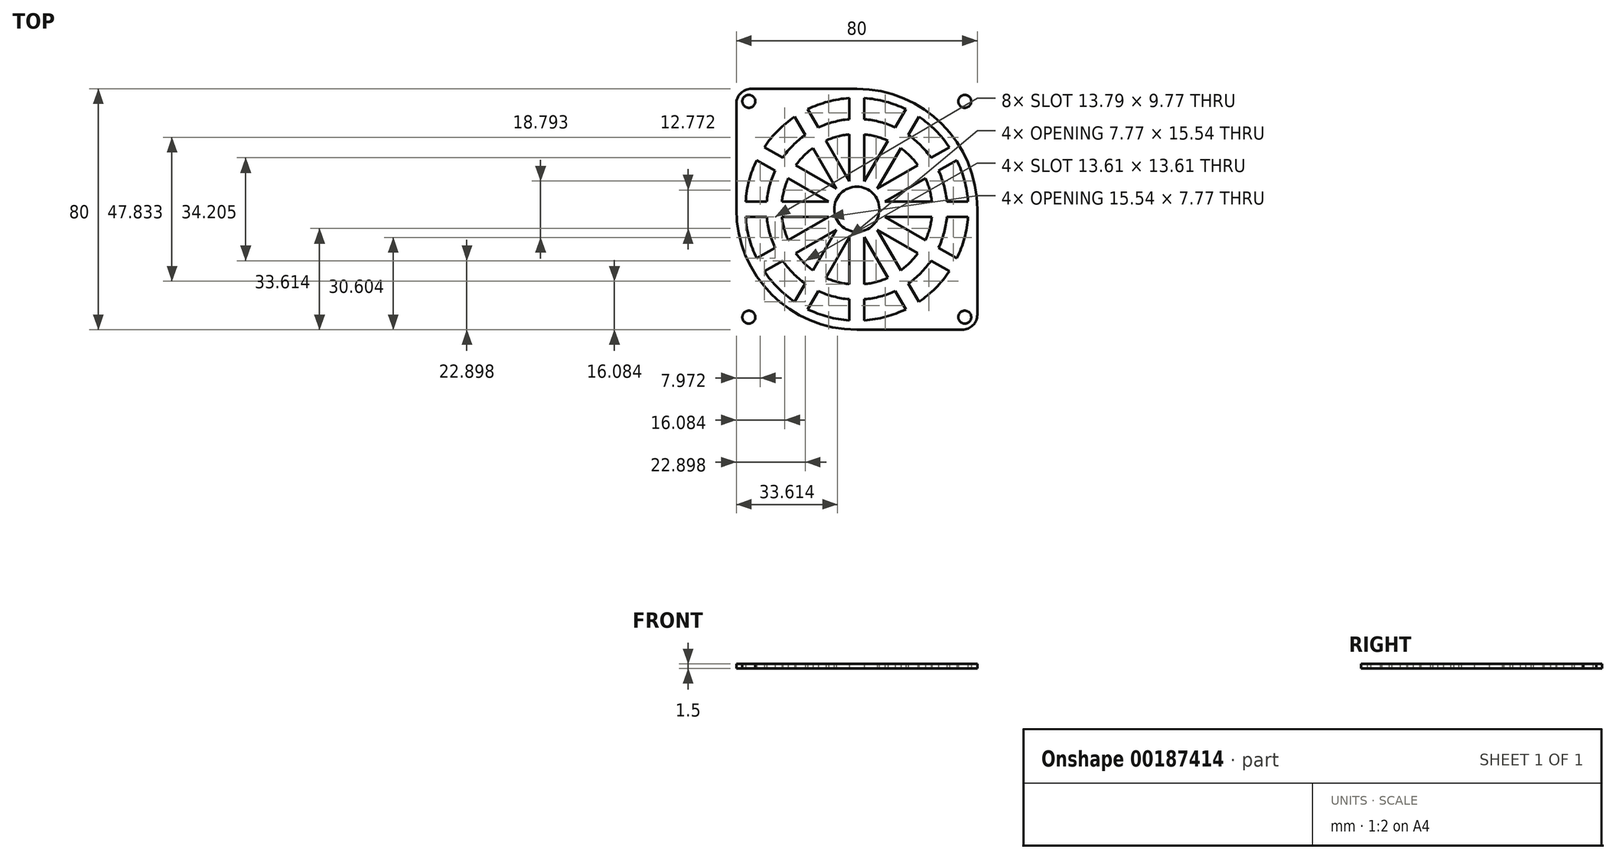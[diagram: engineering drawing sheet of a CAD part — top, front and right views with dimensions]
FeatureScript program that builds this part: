
annotation { "Feature Type Name" : "Feature", "Feature Type Description" : "" }
export const myFeature = defineFeature(function(context is Context, id is Id, definition is map)
    precondition{}
    {
        {
            var Q0;
            Q0=qCreatedBy(makeId("Top.planeOp"),FACE);
            var sketch = newSketch(context, id + "F0", { "sketchPlane" : qUnion([Q0])});
            skLineSegment(sketch, "E0.bottom", {"start": v(-35, 40) * mm, "end": v(35, 40) * mm});
            skLineSegment(sketch, "E0.top", {"start": v(-35, -40) * mm, "end": v(35, -40) * mm});
            skLineSegment(sketch, "E0.left", {"start": v(-40, 35) * mm, "end": v(-40, -35) * mm});
            skLineSegment(sketch, "E0.right", {"start": v(40, 35) * mm, "end": v(40, -35) * mm});
            skPoint(sketch, "E0.middle", {"position": v(0, 0) * mm});
            skCircle(sketch, "E1", {"center": v(0, 0) * mm, "radius": 40 * mm});
            skCircle(sketch, "E2", {"center": v(0, 0) * mm, "radius": 37 * mm});
            skLineSegment(sketch, "E3", {"start": v(-2.5, 36.92) * mm, "end": v(-2.5, 9.33) * mm});
            skLineSegment(sketch, "E4.MirrorCS", {"start": v(2.5, 36.92) * mm, "end": v(2.5, 9.33) * mm});
            skLineSegment(sketch, "E5", {"start": v(-36.92, 2.5) * mm, "end": v(-9.33, 2.5) * mm});
            skCircle(sketch, "E6", {"center": v(-35.85, 35.85) * mm, "radius": 2.15 * mm});
            skCircle(sketch, "E7.MirrorC", {"center": v(35.85, 35.85) * mm, "radius": 2.15 * mm});
            skCircle(sketch, "E8.MirrorC", {"center": v(-35.85, -35.85) * mm, "radius": 2.15 * mm});
            skCircle(sketch, "E9.MirrorC", {"center": v(35.85, -35.85) * mm, "radius": 2.15 * mm});
            skLineSegment(sketch, "E10.MirrorCS", {"start": v(-36.92, -2.5) * mm, "end": v(-9.33, -2.5) * mm});
            skPoint(sketch, "E11.visualSharp", {"position": v(-40, 40) * mm});
            skArc(sketch, "E11.filletArc", {"start": v(-35, 40) * mm, "mid": v(-38.54, 38.54) * mm, "end": v(-40, 35) * mm});
            skPoint(sketch, "E12.visualSharp", {"position": v(40, 40) * mm});
            skArc(sketch, "E12.filletArc", {"start": v(40, 35) * mm, "mid": v(38.54, 38.54) * mm, "end": v(35, 40) * mm});
            skPoint(sketch, "E13.visualSharp", {"position": v(40, -40) * mm});
            skArc(sketch, "E13.filletArc", {"start": v(35, -40) * mm, "mid": v(38.54, -38.54) * mm, "end": v(40, -35) * mm});
            skPoint(sketch, "E14.visualSharp", {"position": v(-40, -40) * mm});
            skArc(sketch, "E14.filletArc", {"start": v(-40, -35) * mm, "mid": v(-38.54, -38.54) * mm, "end": v(-35, -40) * mm});
            skLineSegment(sketch, "E15.1.0", {"start": v(16.3, 33.22) * mm, "end": v(2.5, 9.33) * mm});
            skLineSegment(sketch, "E15.1.1", {"start": v(30.72, -20.62) * mm, "end": v(6.83, -6.83) * mm});
            skLineSegment(sketch, "E15.1.2", {"start": v(33.22, -16.3) * mm, "end": v(9.33, -2.5) * mm});
            skLineSegment(sketch, "E15.1.3", {"start": v(20.62, 30.72) * mm, "end": v(6.83, 6.83) * mm});
            skLineSegment(sketch, "E15.2.0", {"start": v(20.62, -30.72) * mm, "end": v(6.83, -6.83) * mm});
            skLineSegment(sketch, "E15.2.1", {"start": v(-33.22, -16.3) * mm, "end": v(-9.33, -2.5) * mm});
            skLineSegment(sketch, "E15.2.2", {"start": v(-30.72, -20.62) * mm, "end": v(-6.83, -6.83) * mm});
            skLineSegment(sketch, "E15.2.3", {"start": v(16.3, -33.22) * mm, "end": v(2.5, -9.33) * mm});
            skLineSegment(sketch, "E15.anchor1", {"start": v(0, 0) * mm, "end": v(-2.5, -36.92) * mm, "construction": true});
            skLineSegment(sketch, "E15.anchor2", {"start": v(0, 0) * mm, "end": v(33.22, 16.3) * mm, "construction": true});
            skLineSegment(sketch, "E16.trimOffspring", {"start": v(9.33, 2.5) * mm, "end": v(33.22, 16.3) * mm});
            skLineSegment(sketch, "E17.trimOffspring", {"start": v(-2.5, 9.33) * mm, "end": v(-16.3, 33.22) * mm});
            skLineSegment(sketch, "E18.trimOffspring", {"start": v(-6.83, 6.83) * mm, "end": v(-30.72, 20.62) * mm});
            skLineSegment(sketch, "E19.trimOffspring", {"start": v(6.83, 6.83) * mm, "end": v(30.72, 20.62) * mm});
            skLineSegment(sketch, "E20.trimOffspring", {"start": v(-6.83, 6.83) * mm, "end": v(-20.62, 30.72) * mm});
            skLineSegment(sketch, "E21.trimOffspring", {"start": v(-6.83, -6.83) * mm, "end": v(-20.62, -30.72) * mm});
            skLineSegment(sketch, "E22.trimOffspring", {"start": v(-9.33, 2.5) * mm, "end": v(-33.22, 16.3) * mm});
            skLineSegment(sketch, "E23.trimOffspring", {"start": v(9.33, -2.5) * mm, "end": v(36.92, -2.5) * mm});
            skLineSegment(sketch, "E24.trimOffspring", {"start": v(-2.5, -9.33) * mm, "end": v(-16.3, -33.22) * mm});
            skLineSegment(sketch, "E25.trimOffspring", {"start": v(-2.5, -9.33) * mm, "end": v(-2.5, -36.92) * mm});
            skLineSegment(sketch, "E26.trimOffspring", {"start": v(2.5, -9.33) * mm, "end": v(2.5, -36.92) * mm});
            skLineSegment(sketch, "E27.trimOffspring", {"start": v(9.33, 2.5) * mm, "end": v(36.92, 2.5) * mm});
            skSolve(sketch);
        }
        {
            var Q0;
            Q0=qCreatedBy(makeId("Top.planeOp"),FACE);
            var sketch = newSketch(context, id + "F1", { "sketchPlane" : qUnion([Q0])});
            skCircle(sketch, "E28", {"center": v(0, 0) * mm, "radius": 30 * mm});
            skCircle(sketch, "E29", {"center": v(0, 0) * mm, "radius": 25 * mm});
            skSolve(sketch);
        }
        {
            var Q0;
            {var subQ21=sQuery(id+"F0.wireOp",EDGE,"E3");Q0=makeQuery(id+"F0.imprint","IMPRINT",FACE,{"disambiguationData":[TD([[makeQuery(id+"F0.imprint","IMPRINT",EDGE,{"derivedFrom":subQ21}),1.0]])]});}
            var Q1;
            Q1=makeQuery(id+"F0.imprint","IMPRINT",FACE,{"disambiguationData":[TD([[makeQuery(id+"F0.imprint","IMPRINT",EDGE,{"derivedFrom":sQuery(id+"F0.wireOp",EDGE,"E6")}),-1.0]])]});
            var Q2;
            {var subQ18=sQuery(id+"F0.wireOp",EDGE,"E1");var subQ24=makeQuery(id+"F0.imprint","INTERSECT",VERTEX,{"derivedFrom":[sQuery(id+"F0.wireOp",EDGE,"E0.bottom"),subQ18]});Q2=makeQuery(id+"F0.imprint","IMPRINT",FACE,{"disambiguationData":[TD([[makeQuery(id+"F0.imprint","IMPRINT",EDGE,{"disambiguationData":[TD([[subQ24,1.0]])],"derivedFrom":subQ18}),1.0]])]});}
            var Q3;
            Q3=makeQuery(id+"F0.imprint","IMPRINT",FACE,{"disambiguationData":[TD([[makeQuery(id+"F0.imprint","IMPRINT",EDGE,{"derivedFrom":sQuery(id+"F0.wireOp",EDGE,"E8.MirrorC")}),1.0]])]});
            var Q4;
            Q4=makeQuery(id+"F0.imprint","IMPRINT",FACE,{"disambiguationData":[TD([[makeQuery(id+"F0.imprint","IMPRINT",EDGE,{"derivedFrom":sQuery(id+"F0.wireOp",EDGE,"E7.MirrorC")}),1.0]])]});
            var Q5;
            Q5=makeQuery(id+"F0.imprint","IMPRINT",FACE,{"disambiguationData":[TD([[makeQuery(id+"F0.imprint","IMPRINT",EDGE,{"derivedFrom":sQuery(id+"F0.wireOp",EDGE,"E9.MirrorC")}),-1.0]])]});
            extrude(context, id + "F2", {"entities" : qUnion([Q0, Q1, Q2, Q3, Q4, Q5]), "depth" : 1.5 * mm});
        }
        {
            var Q0;
            Q0 = qSketchRegion(id + "F1", true);
            extrude(context, id + "F3", {"entities" : qUnion([Q0]), "operationType" : NewBodyOperationType.ADD, "depth" : 1.5 * mm});
        }
        {
            var Q0;
            Q0=makeQuery(id+"F3.boolean.opBoolean","MERGE",FACE,{"derivedFrom":[makeQuery(id+"F2.opExtrude","CAP_FACE",FACE,{"disambiguationData":[OSD([sQuery(id+"F0.wireOp",EDGE,"E0.bottom"),sQuery(id+"F0.wireOp",EDGE,"E0.top"),sQuery(id+"F0.wireOp",EDGE,"E0.left"),sQuery(id+"F0.wireOp",EDGE,"E0.right"),sQuery(id+"F0.wireOp",EDGE,"E2"),sQuery(id+"F0.wireOp",EDGE,"E3"),sQuery(id+"F0.wireOp",EDGE,"E4.MirrorCS"),sQuery(id+"F0.wireOp",EDGE,"E5"),sQuery(id+"F0.wireOp",EDGE,"E6"),sQuery(id+"F0.wireOp",EDGE,"E7.MirrorC"),sQuery(id+"F0.wireOp",EDGE,"E8.MirrorC"),sQuery(id+"F0.wireOp",EDGE,"E9.MirrorC"),sQuery(id+"F0.wireOp",EDGE,"E10.MirrorCS"),sQuery(id+"F0.wireOp",EDGE,"E11.filletArc"),sQuery(id+"F0.wireOp",EDGE,"E12.filletArc"),sQuery(id+"F0.wireOp",EDGE,"E13.filletArc"),sQuery(id+"F0.wireOp",EDGE,"E14.filletArc"),sQuery(id+"F0.wireOp",EDGE,"E15.1.0"),sQuery(id+"F0.wireOp",EDGE,"E15.1.1"),sQuery(id+"F0.wireOp",EDGE,"E15.1.2"),sQuery(id+"F0.wireOp",EDGE,"E15.1.3"),sQuery(id+"F0.wireOp",EDGE,"E15.2.0"),sQuery(id+"F0.wireOp",EDGE,"E15.2.1"),sQuery(id+"F0.wireOp",EDGE,"E15.2.2"),sQuery(id+"F0.wireOp",EDGE,"E15.2.3"),sQuery(id+"F0.wireOp",EDGE,"E16.trimOffspring"),sQuery(id+"F0.wireOp",EDGE,"E17.trimOffspring"),sQuery(id+"F0.wireOp",EDGE,"E18.trimOffspring"),sQuery(id+"F0.wireOp",EDGE,"E19.trimOffspring"),sQuery(id+"F0.wireOp",EDGE,"E20.trimOffspring"),sQuery(id+"F0.wireOp",EDGE,"E21.trimOffspring"),sQuery(id+"F0.wireOp",EDGE,"E22.trimOffspring"),sQuery(id+"F0.wireOp",EDGE,"E23.trimOffspring"),sQuery(id+"F0.wireOp",EDGE,"E24.trimOffspring"),sQuery(id+"F0.wireOp",EDGE,"E25.trimOffspring"),sQuery(id+"F0.wireOp",EDGE,"E26.trimOffspring"),sQuery(id+"F0.wireOp",EDGE,"E27.trimOffspring")])],"isStart":false}),makeQuery(id+"F3.opExtrude","CAP_FACE",FACE,{"disambiguationData":[OSD([sQuery(id+"F1.wireOp",EDGE,"E28"),sQuery(id+"F1.wireOp",EDGE,"E29")])],"isStart":false})]});
            var sketch = newSketch(context, id + "F4", { "sketchPlane" : qUnion([Q0])});
            skCircle(sketch, "E30", {"center": v(0, 0) * mm, "radius": 7.5 * mm});
            skSolve(sketch);
        }
        {
            var Q0;
            Q0=makeQuery(id+"F4.imprint","IMPRINT",FACE,{"disambiguationData":[TD([[makeQuery(id+"F4.imprint","IMPRINT",EDGE,{"derivedFrom":sQuery(id+"F4.wireOp",EDGE,"E30")}),1.0]])]});
            extrude(context, id + "F5", {"entities" : qUnion([Q0]), "operationType" : NewBodyOperationType.REMOVE, "oppositeDirection" : true, "depth" : 25 * mm});
        }
    });
